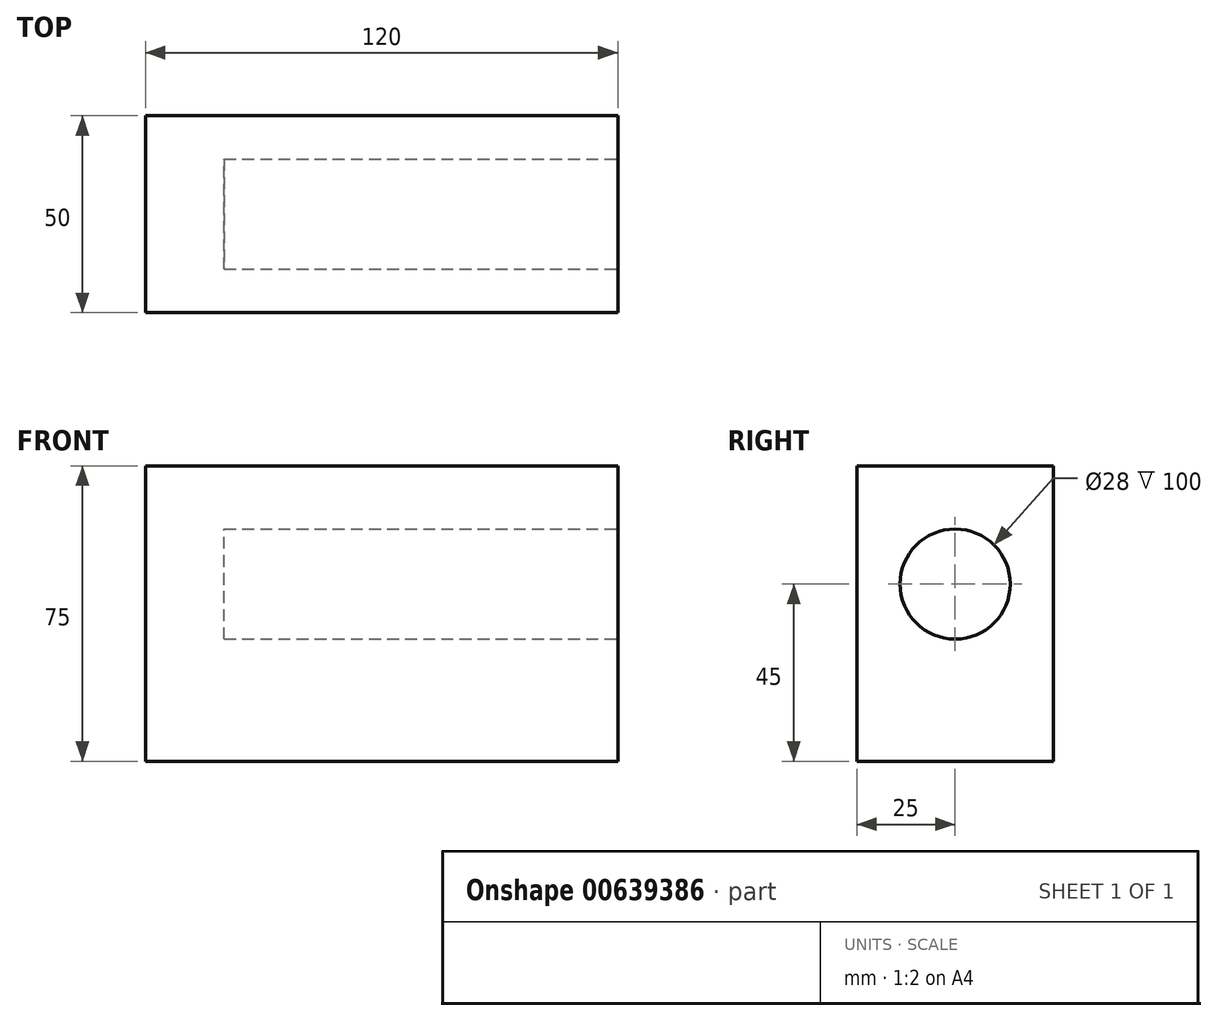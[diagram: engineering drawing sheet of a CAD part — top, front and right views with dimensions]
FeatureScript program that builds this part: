
annotation { "Feature Type Name" : "Feature", "Feature Type Description" : "" }
export const myFeature = defineFeature(function(context is Context, id is Id, definition is map)
    precondition{}
    {
        {
            var Q0;
            Q0=qCreatedBy(makeId("Front.planeOp"),FACE);
            var sketch = newSketch(context, id + "F0", { "sketchPlane" : qUnion([Q0])});
            skLineSegment(sketch, "E0.bottom", {"start": v(0, 0) * mm, "end": v(120, 0) * mm});
            skLineSegment(sketch, "E0.top", {"start": v(0, 75) * mm, "end": v(120, 75) * mm});
            skLineSegment(sketch, "E0.left", {"start": v(0, 0) * mm, "end": v(0, 75) * mm});
            skLineSegment(sketch, "E0.right", {"start": v(120, 0) * mm, "end": v(120, 75) * mm});
            skLineSegment(sketch, "E1.bottom", {"start": v(120, 37.5) * mm, "end": v(120, 37.5) * mm});
            skLineSegment(sketch, "E1.top", {"start": v(120, 37.5) * mm, "end": v(120, 37.5) * mm});
            skLineSegment(sketch, "E1.left", {"start": v(120, 37.5) * mm, "end": v(120, 37.5) * mm});
            skLineSegment(sketch, "E1.right", {"start": v(120, 37.5) * mm, "end": v(120, 37.5) * mm});
            skSolve(sketch);
        }
        {
            var Q0;
            Q0 = qSketchRegion(id + "F0", true);
            extrude(context, id + "F1", {"entities" : qUnion([Q0]), "depth" : 50 * mm, "offsetDistance" : 25 * mm});
        }
        {
            var Q0;
            Q0=makeQuery(id+"F1.opExtrude","SWEPT_FACE",FACE,{"disambiguationData":[OSD([sQuery(id+"F0.wireOp",EDGE,"E0.right")])]});
            var sketch = newSketch(context, id + "F2", { "sketchPlane" : qUnion([Q0])});
            skCircle(sketch, "E2", {"center": v(-25, 45) * mm, "radius": 14 * mm});
            skPoint(sketch, "E2.centerSnap0", {"position": v(-25, 75) * mm});
            skSolve(sketch);
        }
        {
            var Q0;
            Q0 = qSketchRegion(id + "F2", true);
            extrude(context, id + "F3", {"entities" : qUnion([Q0]), "operationType" : NewBodyOperationType.REMOVE, "oppositeDirection" : true, "depth" : 100 * mm, "offsetDistance" : 25 * mm});
        }
    });
